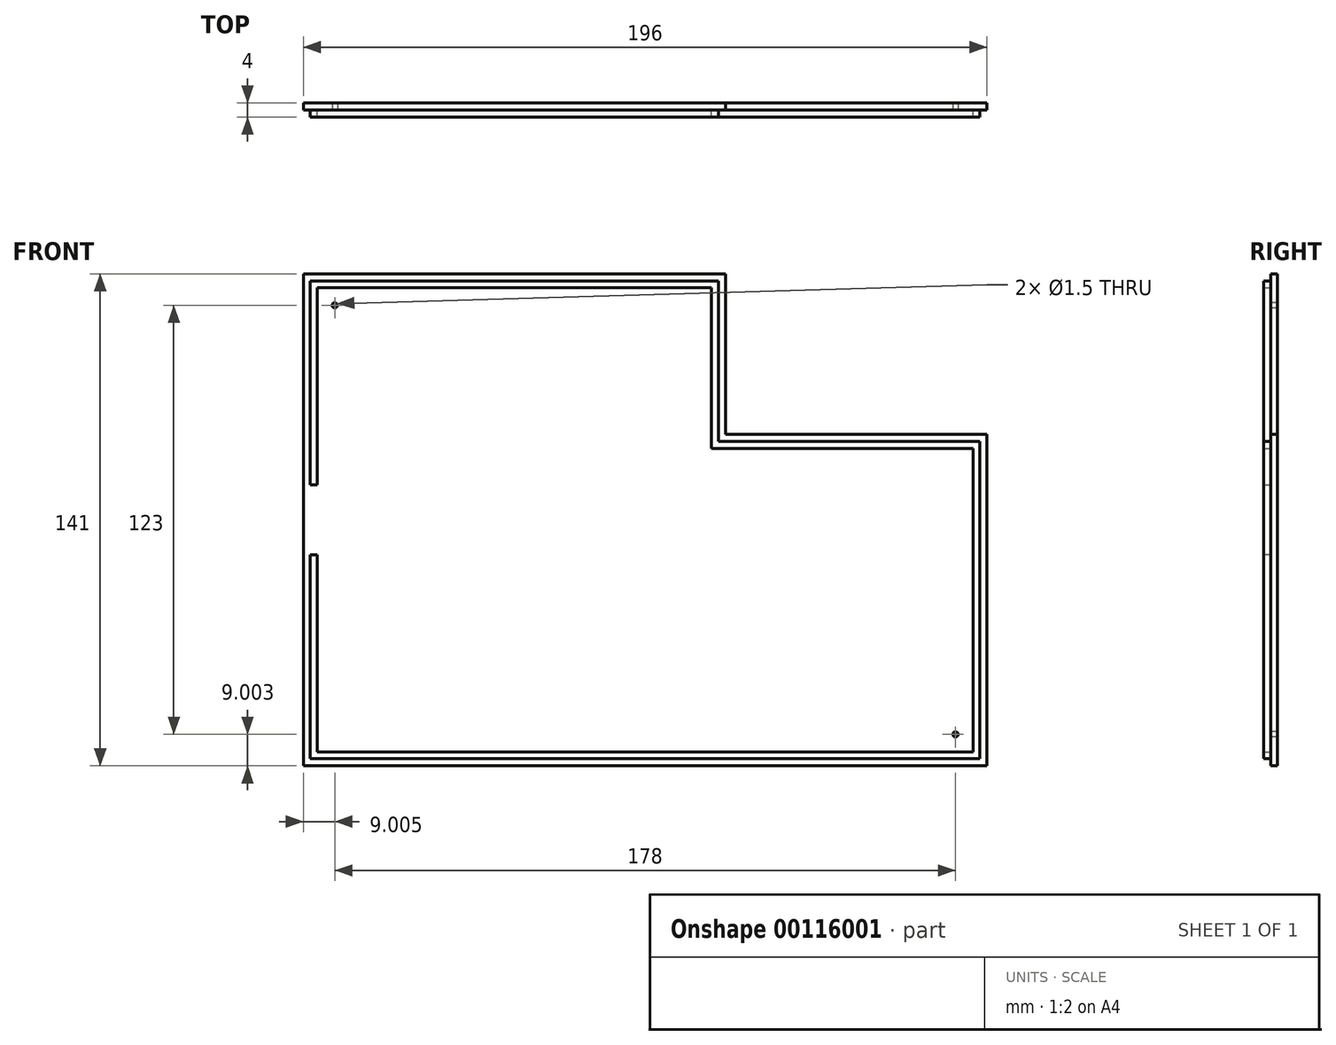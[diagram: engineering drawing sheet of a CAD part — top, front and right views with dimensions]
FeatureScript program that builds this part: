
annotation { "Feature Type Name" : "Feature", "Feature Type Description" : "" }
export const myFeature = defineFeature(function(context is Context, id is Id, definition is map)
    precondition{}
    {
        {
            var Q0;
            Q0=qCreatedBy(makeId("Front.planeOp"),FACE);
            var sketch = newSketch(context, id + "F0", { "sketchPlane" : qUnion([Q0])});
            skLineSegment(sketch, "E0.bottom", {"start": v(-6.34, -62.27) * mm, "end": v(-127.34, -62.27) * mm});
            skLineSegment(sketch, "E0.top", {"start": v(-6.34, 78.73) * mm, "end": v(-127.34, 78.73) * mm});
            skLineSegment(sketch, "E0.left", {"start": v(-6.34, -62.27) * mm, "end": v(-6.34, 78.73) * mm});
            skLineSegment(sketch, "E0.right", {"start": v(-127.34, -62.27) * mm, "end": v(-127.34, 78.73) * mm});
            skLineSegment(sketch, "E1.bottom", {"start": v(-6.34, -62.27) * mm, "end": v(68.66, -62.27) * mm});
            skLineSegment(sketch, "E1.top", {"start": v(-6.34, 32.73) * mm, "end": v(68.66, 32.73) * mm});
            skLineSegment(sketch, "E1.left", {"start": v(-6.34, -62.27) * mm, "end": v(-6.34, 32.73) * mm});
            skLineSegment(sketch, "E1.right", {"start": v(68.66, -62.27) * mm, "end": v(68.66, 32.73) * mm});
            skSolve(sketch);
        }
        {
            var Q0;
            Q0=makeQuery(id+"F0.imprint","IMPRINT",FACE,{"disambiguationData":[TD([[makeQuery(id+"F0.imprint","IMPRINT",EDGE,{"derivedFrom":sQuery(id+"F0.wireOp",EDGE,"E0.bottom")}),-1.0]])]});
            var Q1;
            Q1=makeQuery(id+"F0.imprint","IMPRINT",FACE,{"disambiguationData":[TD([[makeQuery(id+"F0.imprint","IMPRINT",EDGE,{"derivedFrom":sQuery(id+"F0.wireOp",EDGE,"E1.bottom")}),1.0]])]});
            extrude(context, id + "F1", {"entities" : qUnion([Q0, Q1]), "depth" : 2 * mm});
        }
        {
            var Q0;
            Q0=makeQuery(id+"F1.opExtrude","CAP_FACE",FACE,{"disambiguationData":[OSD([sQuery(id+"F0.wireOp",EDGE,"E0.bottom"),sQuery(id+"F0.wireOp",EDGE,"E0.top"),sQuery(id+"F0.wireOp",EDGE,"E0.left"),sQuery(id+"F0.wireOp",EDGE,"E0.right"),sQuery(id+"F0.wireOp",EDGE,"E1.bottom"),sQuery(id+"F0.wireOp",EDGE,"E1.top"),sQuery(id+"F0.wireOp",EDGE,"E1.right")])],"isStart":false});
            var sketch = newSketch(context, id + "F2", { "sketchPlane" : qUnion([Q0])});
            skLineSegment(sketch, "E2.bottom", {"start": v(-125.34, 76.73) * mm, "end": v(-123.34, 76.73) * mm});
            skLineSegment(sketch, "E2.top", {"start": v(-125.34, -60.27) * mm, "end": v(-123.34, -60.27) * mm});
            skLineSegment(sketch, "E2.left", {"start": v(-125.34, 76.73) * mm, "end": v(-125.34, -60.27) * mm});
            skLineSegment(sketch, "E2.right", {"start": v(-123.34, 76.73) * mm, "end": v(-123.34, -60.27) * mm});
            skLineSegment(sketch, "E3.bottom", {"start": v(-123.34, 76.73) * mm, "end": v(-8.34, 76.73) * mm});
            skLineSegment(sketch, "E3.top", {"start": v(-123.34, 74.73) * mm, "end": v(-8.34, 74.73) * mm});
            skLineSegment(sketch, "E3.left", {"start": v(-123.34, 76.73) * mm, "end": v(-123.34, 74.73) * mm});
            skLineSegment(sketch, "E3.right", {"start": v(-8.34, 76.73) * mm, "end": v(-8.34, 74.73) * mm});
            skLineSegment(sketch, "E4.bottom", {"start": v(-8.34, 74.73) * mm, "end": v(-10.34, 74.73) * mm});
            skLineSegment(sketch, "E4.top", {"start": v(-8.34, 28.73) * mm, "end": v(-10.34, 28.73) * mm});
            skLineSegment(sketch, "E4.left", {"start": v(-8.34, 74.73) * mm, "end": v(-8.34, 28.73) * mm});
            skLineSegment(sketch, "E4.right", {"start": v(-10.34, 74.73) * mm, "end": v(-10.34, 28.73) * mm});
            skLineSegment(sketch, "E5.bottom", {"start": v(-8.34, 28.73) * mm, "end": v(66.66, 28.73) * mm});
            skLineSegment(sketch, "E5.top", {"start": v(-8.34, 30.73) * mm, "end": v(66.66, 30.73) * mm});
            skLineSegment(sketch, "E5.left", {"start": v(-8.34, 28.73) * mm, "end": v(-8.34, 30.73) * mm});
            skLineSegment(sketch, "E5.right", {"start": v(66.66, 28.73) * mm, "end": v(66.66, 30.73) * mm});
            skLineSegment(sketch, "E6.bottom", {"start": v(66.66, 28.73) * mm, "end": v(64.66, 28.73) * mm});
            skLineSegment(sketch, "E6.top", {"start": v(66.66, -60.27) * mm, "end": v(64.66, -60.27) * mm});
            skLineSegment(sketch, "E6.left", {"start": v(66.66, 28.73) * mm, "end": v(66.66, -60.27) * mm});
            skLineSegment(sketch, "E6.right", {"start": v(64.66, 28.73) * mm, "end": v(64.66, -60.27) * mm});
            skLineSegment(sketch, "E7.bottom", {"start": v(64.66, -60.27) * mm, "end": v(-123.34, -60.27) * mm});
            skLineSegment(sketch, "E7.top", {"start": v(64.66, -58.27) * mm, "end": v(-123.34, -58.27) * mm});
            skLineSegment(sketch, "E7.left", {"start": v(64.66, -60.27) * mm, "end": v(64.66, -58.27) * mm});
            skLineSegment(sketch, "E7.right", {"start": v(-123.34, -60.27) * mm, "end": v(-123.34, -58.27) * mm});
            skSolve(sketch);
        }
        {
            var Q0;
            Q0 = qSketchRegion(id + "F2", true);
            extrude(context, id + "F3", {"entities" : qUnion([Q0]), "operationType" : NewBodyOperationType.ADD, "depth" : 2 * mm});
        }
        {
            var Q0;
            Q0=makeQuery(id+"F3.boolean.opBoolean","SPLIT",FACE,{"disambiguationData":[TD([makeQuery(id+"F3.opExtrude","SWEPT_FACE",FACE,{"disambiguationData":[OSD([sQuery(id+"F2.wireOp",EDGE,"E2.right")])]})])],"derivedFrom":makeQuery(id+"F1.opExtrude","CAP_FACE",FACE,{"disambiguationData":[OSD([sQuery(id+"F0.wireOp",EDGE,"E0.bottom"),sQuery(id+"F0.wireOp",EDGE,"E0.top"),sQuery(id+"F0.wireOp",EDGE,"E0.left"),sQuery(id+"F0.wireOp",EDGE,"E0.right"),sQuery(id+"F0.wireOp",EDGE,"E1.bottom"),sQuery(id+"F0.wireOp",EDGE,"E1.top"),sQuery(id+"F0.wireOp",EDGE,"E1.right")])],"isStart":false})});
            var sketch = newSketch(context, id + "F4", { "sketchPlane" : qUnion([Q0])});
            skCircle(sketch, "E8", {"center": v(59.66, -53.27) * mm, "radius": 3.52 * mm});
            skCircle(sketch, "E9", {"center": v(-118.34, 69.73) * mm, "radius": 3.5 * mm});
            skSolve(sketch);
        }
        {
            var Q0;
            Q0=sQuery(id+"F4.wireOp",VERTEX,"E9.center");
            var Q1;
            Q1=sQuery(id+"F4.wireOp",VERTEX,"E8.center");
            var Q2;
            Q2=makeQuery(id+"F1.opExtrude","SWEPT_BODY",BODY,{"disambiguationData":[OSD([sQuery(id+"F0.wireOp",EDGE,"E0.bottom"),sQuery(id+"F0.wireOp",EDGE,"E0.top"),sQuery(id+"F0.wireOp",EDGE,"E0.left"),sQuery(id+"F0.wireOp",EDGE,"E0.right"),sQuery(id+"F0.wireOp",EDGE,"E1.bottom"),sQuery(id+"F0.wireOp",EDGE,"E1.top"),sQuery(id+"F0.wireOp",EDGE,"E1.right")])]});
            hole(context, id + "F5", {"style" : HoleStyle.SIMPLE, "endStyle" : HoleEndStyle.BLIND, "holeDiameter" : 1.5 * mm, "holeDepth" : 2 * mm, "locations" : qUnion([Q0, Q1]), "scope" : qUnion([Q2])});
        }
        {
            var Q0;
            Q0=makeQuery(id+"F3.opExtrude","SWEPT_FACE",FACE,{"disambiguationData":[OSD([sQuery(id+"F2.wireOp",EDGE,"E2.left")])]});
            var sketch = newSketch(context, id + "F6", { "sketchPlane" : qUnion([Q0])});
            skLineSegment(sketch, "E10.bottom", {"start": v(2, 18.23) * mm, "end": v(4, 18.23) * mm});
            skLineSegment(sketch, "E10.top", {"start": v(2, -1.77) * mm, "end": v(4, -1.77) * mm});
            skLineSegment(sketch, "E10.left", {"start": v(2, 18.23) * mm, "end": v(2, -1.77) * mm});
            skLineSegment(sketch, "E10.right", {"start": v(4, 18.23) * mm, "end": v(4, -1.77) * mm});
            skSolve(sketch);
        }
        {
            var Q0;
            {var subQ0=sQuery(id+"F6.wireOp",EDGE,"E10.left");Q0=makeQuery(id+"F6.imprint","IMPRINT",FACE,{"disambiguationData":[TD([[makeQuery(id+"F6.imprint","IMPRINT",EDGE,{"derivedFrom":subQ0}),1.0]])]});}
            extrude(context, id + "F7", {"entities" : qUnion([Q0]), "operationType" : NewBodyOperationType.REMOVE, "oppositeDirection" : true, "depth" : 25 * mm});
        }
    });
